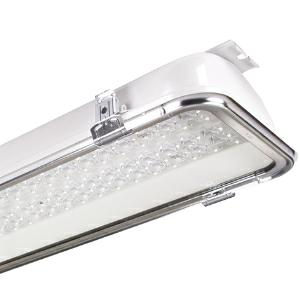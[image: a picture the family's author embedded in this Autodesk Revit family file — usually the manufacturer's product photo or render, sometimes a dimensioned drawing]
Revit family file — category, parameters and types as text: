
# Revit family: 3f_filippi_-_beta_235_76_vt_concentrato_3f_filippi_-_52526_-_beta_235_led_762x45_conc_vt_l1265
name_source: partatom
category: Lighting Fixtures
units: mm (PartAtom-declared; Revit-internal decimal feet)

## family parameters
Cut with Voids When Loaded = No
Host = Face
Light Source = No
Part Type = Normal
Room Calculation Point = No
Round Connector Dimension = Use Diameter
Shared = No

## types (1)
- 3F Filippi - Beta 235 76 VT Concentrato (1 x LED, 13693 lm, 92 W, 4000 K)
    Apparent Load = 92 VA
    Approval mark = CE
    CIE Flux Codes = 76 93 99 100 100
    Color Rendering = 80
    Color Temperature = 4000 K
    Control Gear = Electronic ballast
    Default Elevation = 1800 mm
    Description = ILLUMINOTECHNICAL
Luminous efficiency 100% (DLOR 100%, ULOR 0%).
Initial luminous flux of the luminaire 13693 lm.
Concentrated elliptical distribution.
Installation Interdistance Transv.D = 0.58 x hu - Long.D = 1.12 x hu.
Tabular UGR (CIE 117 - 4H-8H; S=0.25H; 70/50/20): RUG 18.9 - 21.4.
Beam angle: 36° - 73°.
Luminous efficacy 149 lm/W.
Lifetime (L93/B10): 30000 h. (tq+25°C)
Lifetime (L90/B10): 50000 h. (tq+25°C)
Lifetime (L85/B10): 80000 h. (tq+25°C)
Lifetime (L80/B10): 100000 h. (tq+25°C)
Lifetime (L85/B10): 50000 h. (tq+45°C)
Sudden decreased luminous flux after 50000 hours: 0% (C0).
Photobiological safety in compliance with IEC/TR 62778: RG0 risk exempt, (IEC 62471).
In compliance with IEC/EN 62722-2-1 - IEC/EN 62717 standards.

SOURCE
2 linear LED modules 45W/840.
Energy efficiency class (UE 2019/2020 - UE 2019/2015): C.
CIE 13.3 Colour rendering index: CRI >80 (R9 <50%).
IES TM-30 Fidelity Index: Rf = 84 Rg = 95.
CCT nominal colour temperature 4000 K.
Colour initial tolerance (MacAdam): SDCM 3.

MECHANICAL
Single-piece housing in pressed steel, powder-coated in white epoxy-polyester.
VT transparent glass, non-combustible, single-piece perimeter frame in galvanised steel.
Ecologic anti-aging injected sealing gasket.
Oversized gear-tray reflector unit in highly reflective white painted hot-galvanised steel.
Methacrylate (PMMA) lenses with external flat surface.
Galvanised steel snap-lock clips for diffuser mounting (safety n° 4 per fixture).
Luminaire with limited surface temperature. - D - (EN 60598-2-24)
Dimensions: 1265x235 mm, height 105 mm. Weight 10.05 kg.
IP66 protection degree.
Mechanical strength to impacts IK09 (10 joule).
Glow-wire test resistance 850°C.

ELECTRICAL
Halogen Free electronic wiring 230V-50/60Hz, power factor 0.95, THD <25%, constant output current, class I, 1 driver.
Power of the luminaire 92 W.
ENEC - CE.
Flicker: <4%.
Luminaire compliant with EN 60598-2-22 for power supply from a centralised emergency system CPSS (Central Power Supply System), not incorporated in the luminaire - high risk areas excluded. The default power and flux are 100% in AC and 100% in DC.
Ambient temperature from -20°C to +45°C.
Temperature class T6 max 85°C.
Quick connection via M20 3P connector with 9-13 mm tightening range.
Relative humidity UR: <85%.

INSTALLATION
Ceiling / Suspended / Wall.
All accessories dedicated to this product are available on the Catalog and on our website www.3F-Filippi.com.

APPLICATIONS
Dry, dusty indoor environments, subject to occasional water splashes.
Industrial environments, warehouses, environments where security locks are required on all clips, e.g. prisons (on request).
Environments in which it is necessary a total protection against falling fragments (eg environments with foodstuffs or machines with moving parts or with extreme temperature changes), use luminaires with laminated glass.
Tempered glass is not immune to falling fragments from harmless and caused by shocks or exceptionally derived from the tempering process.

WARNING
Fixture not suitable for cold stores with an ambient temperature <0°C and/or relative humidity >85%.
Luminaire designed for disposal/recycling at end-of-life.
Replaceable (LED only) light source by a professional. Replaceable control gear by a professional.
    Height = 105 mm
    Lamp = 1 x LED
    Lamp Light Flux = 13693 lm
    Lamp Power = 92 W
    Lamp count = 1
    Length = 1265 mm
    Lifetime = 50000 h
    Luminous efficacy = 149 lm/W
    Manufacturer = 3F Filippi
    ModVariant = No
    Model = 3F Filippi - 52526 - Beta 235 LED 762x45 CONC VT L1265
    Mounting Place = Ceiling
    Mounting Type = Pendant
    Number of Poles = 1
    OnlyDefault = Yes
    Power Factor = 1
    Product Name = 3F Filippi - Beta 235 76 VT Concentrato
    Product group = pendant luminaire
    ProductGroupID = 9
    Protection Class = Protection class I
    Protection Degree = IP 66
    RLX_Detail_Level = 1
    RLX_Emergency_Light_Flux = 0 lm
    RLX_Emergency_Type = 0
    RLX_Emergency_Type_DB = No
    RlxData = <blob elided: 90089 chars, md5=171a9c83>
    Socket = socket
    Standby Power = 0 W
    System Light Flux = 13693 lm
    System Power = 92 W
    Type Comments = Product without accessories
    Type Image = 3ffilippi_beta_235_led_76_vt.jpg
    URL = http://relux.com
    VarID = ---
    Voltage = 0 V
    Weight = 0.00 kg
    Width = 235 mm

## geometry (parser evidence)
native form markers: Blend x4, Sweep x11
no freeform markers — native parametric forms only
